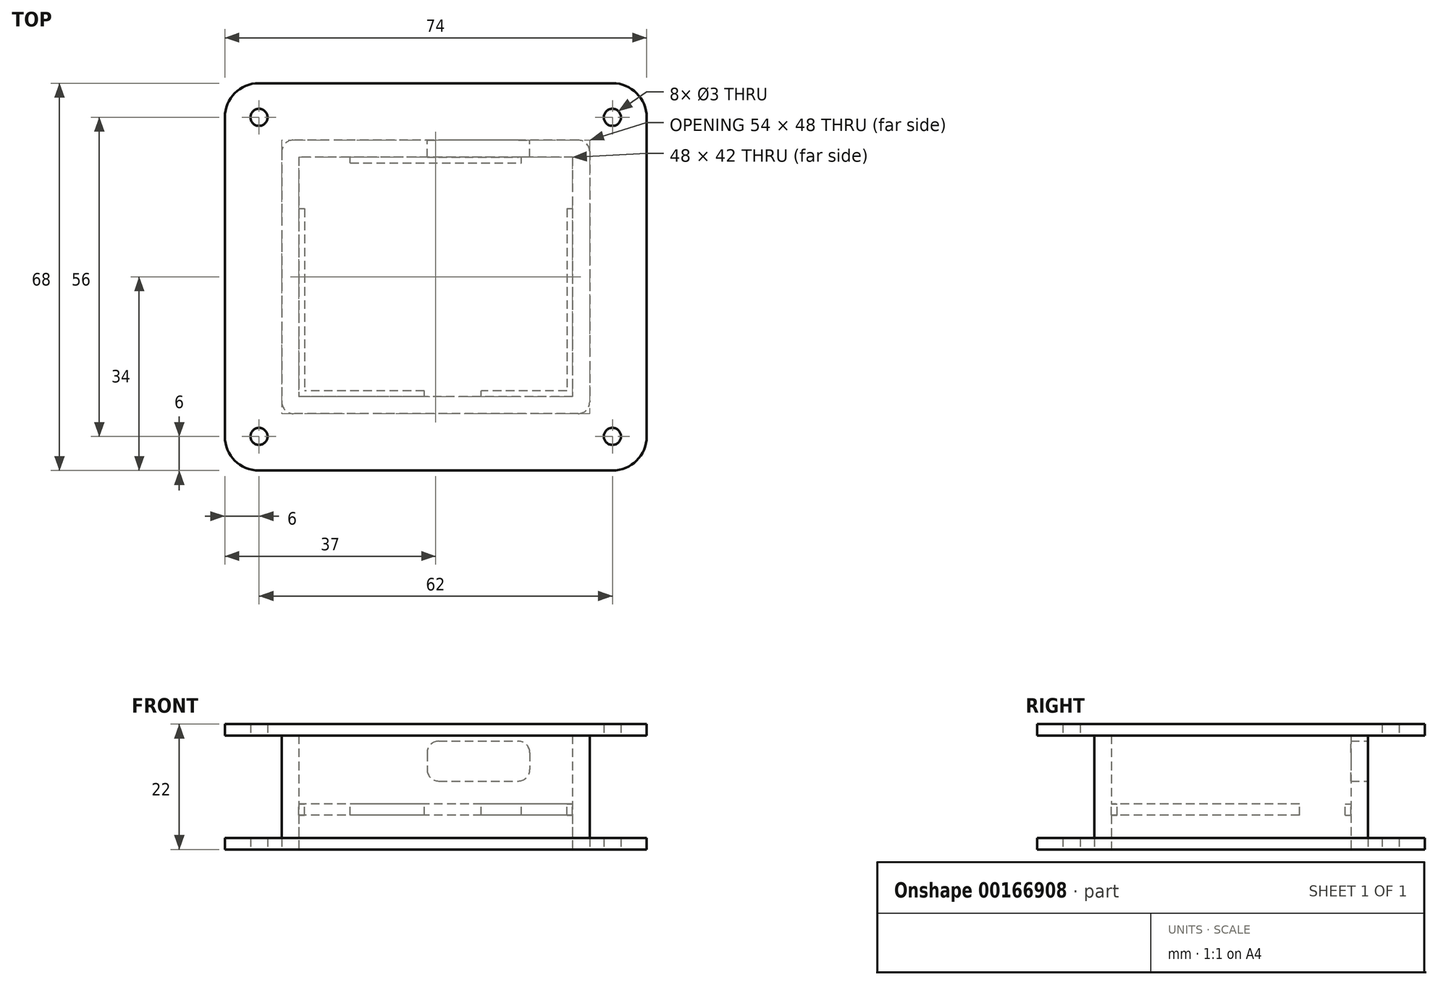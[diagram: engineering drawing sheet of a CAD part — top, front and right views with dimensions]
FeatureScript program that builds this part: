
annotation { "Feature Type Name" : "Feature", "Feature Type Description" : "" }
export const myFeature = defineFeature(function(context is Context, id is Id, definition is map)
    precondition{}
    {
        {
            var Q0;
            Q0=qCreatedBy(makeId("Top.planeOp"),FACE);
            var sketch = newSketch(context, id + "F0", { "sketchPlane" : qUnion([Q0])});
            skLineSegment(sketch, "E0.bottom", {"start": v(24, 21) * mm, "end": v(-24, 21) * mm});
            skLineSegment(sketch, "E0.top", {"start": v(24, -21) * mm, "end": v(-24, -21) * mm});
            skLineSegment(sketch, "E0.left", {"start": v(24, 21) * mm, "end": v(24, -21) * mm});
            skLineSegment(sketch, "E0.right", {"start": v(-24, 21) * mm, "end": v(-24, -21) * mm});
            skPoint(sketch, "E0.middle", {"position": v(0, 0) * mm});
            skLineSegment(sketch, "E1.0", {"start": v(-27, 22) * mm, "end": v(-27, -22) * mm});
            skLineSegment(sketch, "E1.1", {"start": v(25, 24) * mm, "end": v(-25, 24) * mm});
            skLineSegment(sketch, "E1.2", {"start": v(27, 22) * mm, "end": v(27, -22) * mm});
            skLineSegment(sketch, "E1.3", {"start": v(25, -24) * mm, "end": v(-25, -24) * mm});
            skPoint(sketch, "E2.visualSharp", {"position": v(-27, 24) * mm});
            skArc(sketch, "E2.filletArc", {"start": v(-25, 24) * mm, "mid": v(-26.41, 23.41) * mm, "end": v(-27, 22) * mm});
            skPoint(sketch, "E3.visualSharp", {"position": v(-27, -24) * mm});
            skArc(sketch, "E3.filletArc", {"start": v(-27, -22) * mm, "mid": v(-26.41, -23.41) * mm, "end": v(-25, -24) * mm});
            skPoint(sketch, "E4.visualSharp", {"position": v(27, -24) * mm});
            skArc(sketch, "E4.filletArc", {"start": v(25, -24) * mm, "mid": v(26.41, -23.41) * mm, "end": v(27, -22) * mm});
            skPoint(sketch, "E5.visualSharp", {"position": v(27, 24) * mm});
            skArc(sketch, "E5.filletArc", {"start": v(27, 22) * mm, "mid": v(26.41, 23.41) * mm, "end": v(25, 24) * mm});
            skSolve(sketch);
        }
        {
            var Q0;
            Q0 = qSketchRegion(id + "F0", true);
            extrude(context, id + "F1", {"entities" : qUnion([Q0]), "depth" : 20 * mm});
        }
        {
            var Q0;
            Q0=makeQuery(id+"F1.opExtrude","SWEPT_FACE",FACE,{"disambiguationData":[OSD([sQuery(id+"F0.wireOp",EDGE,"E1.1")])]});
            var sketch = newSketch(context, id + "F2", { "sketchPlane" : qUnion([Q0])});
            skLineSegment(sketch, "E6", {"start": v(-32.33, 8) * mm, "end": v(34.44, 8) * mm, "construction": true});
            skLineSegment(sketch, "E7", {"start": v(-32.34, 10) * mm, "end": v(33.7, 10) * mm, "construction": true});
            skLineSegment(sketch, "E8.bottom", {"start": v(-14.5, 12) * mm, "end": v(-0.5, 12) * mm});
            skLineSegment(sketch, "E8.top", {"start": v(-14.5, 19) * mm, "end": v(-0.5, 19) * mm});
            skLineSegment(sketch, "E8.left", {"start": v(-16.5, 14) * mm, "end": v(-16.5, 17) * mm});
            skLineSegment(sketch, "E8.right", {"start": v(1.5, 14) * mm, "end": v(1.5, 17) * mm});
            skLineSegment(sketch, "E9", {"start": v(-16.5, 19) * mm, "end": v(1.5, 12) * mm, "construction": true});
            skLineSegment(sketch, "E10", {"start": v(-16.5, 12) * mm, "end": v(1.5, 19) * mm, "construction": true});
            skPoint(sketch, "E11", {"position": v(-7.5, 15.5) * mm});
            skPoint(sketch, "E12.visualSharp", {"position": v(-16.5, 19) * mm});
            skArc(sketch, "E12.filletArc", {"start": v(-14.5, 19) * mm, "mid": v(-15.91, 18.41) * mm, "end": v(-16.5, 17) * mm});
            skPoint(sketch, "E13.visualSharp", {"position": v(-16.5, 12) * mm});
            skArc(sketch, "E13.filletArc", {"start": v(-16.5, 14) * mm, "mid": v(-15.91, 12.59) * mm, "end": v(-14.5, 12) * mm});
            skPoint(sketch, "E14.visualSharp", {"position": v(1.5, 12) * mm});
            skArc(sketch, "E14.filletArc", {"start": v(-0.5, 12) * mm, "mid": v(0.91, 12.59) * mm, "end": v(1.5, 14) * mm});
            skPoint(sketch, "E15.visualSharp", {"position": v(1.5, 19) * mm});
            skArc(sketch, "E15.filletArc", {"start": v(1.5, 17) * mm, "mid": v(0.91, 18.41) * mm, "end": v(-0.5, 19) * mm});
            skSolve(sketch);
        }
        {
            var Q0;
            Q0 = qSketchRegion(id + "F2", true);
            extrude(context, id + "F3", {"entities" : qUnion([Q0]), "operationType" : NewBodyOperationType.REMOVE, "oppositeDirection" : true, "depth" : 25 * mm});
        }
        {
            var Q0;
            Q0=makeQuery(id+"F1.opExtrude","CAP_FACE",FACE,{"disambiguationData":[OSD([sQuery(id+"F0.wireOp",EDGE,"E0.bottom"),sQuery(id+"F0.wireOp",EDGE,"E0.top"),sQuery(id+"F0.wireOp",EDGE,"E0.left"),sQuery(id+"F0.wireOp",EDGE,"E0.right"),sQuery(id+"F0.wireOp",EDGE,"E1.0"),sQuery(id+"F0.wireOp",EDGE,"E1.1"),sQuery(id+"F0.wireOp",EDGE,"E1.2"),sQuery(id+"F0.wireOp",EDGE,"E1.3"),sQuery(id+"F0.wireOp",EDGE,"E2.filletArc"),sQuery(id+"F0.wireOp",EDGE,"E3.filletArc"),sQuery(id+"F0.wireOp",EDGE,"E4.filletArc"),sQuery(id+"F0.wireOp",EDGE,"E5.filletArc")])],"isStart":false});
            cPlane(context, id + "F4", {"entities" : qUnion([Q0]), "cplaneType" : CPlaneType.OFFSET, "offset" : 12 * mm, "oppositeDirection" : true, "width" : 150 * mm, "height" : 150 * mm});
        }
        {
            var Q0;
            Q0=qCreatedBy(id+"F4.planeOp",FACE);
            var sketch = newSketch(context, id + "F5", { "sketchPlane" : qUnion([Q0])});
            skLineSegment(sketch, "E16.0", {"start": v(24, 12) * mm, "end": v(24, -21) * mm});
            skLineSegment(sketch, "E16.1", {"start": v(24, -21) * mm, "end": v(8, -21) * mm});
            skLineSegment(sketch, "E16.2", {"start": v(15, 21) * mm, "end": v(-15, 21) * mm});
            skLineSegment(sketch, "E16.3", {"start": v(-24, 12) * mm, "end": v(-24, -21) * mm});
            skLineSegment(sketch, "E17.0", {"start": v(23, -20) * mm, "end": v(8, -20) * mm});
            skLineSegment(sketch, "E17.1", {"start": v(23, 12) * mm, "end": v(23, -20) * mm});
            skLineSegment(sketch, "E17.3", {"start": v(-23, 12) * mm, "end": v(-23, -20) * mm});
            skLineSegment(sketch, "E18", {"start": v(-24, 12) * mm, "end": v(-23, 12) * mm});
            skLineSegment(sketch, "E19", {"start": v(23, 12) * mm, "end": v(24, 12) * mm});
            skLineSegment(sketch, "E20", {"start": v(-15, 20) * mm, "end": v(-15, 21) * mm});
            skLineSegment(sketch, "E21", {"start": v(15, 20) * mm, "end": v(15, 21) * mm});
            skPoint(sketch, "E22.orphan", {"position": v(-24, 21) * mm});
            skPoint(sketch, "E23.orphan", {"position": v(24, 21) * mm});
            skLineSegment(sketch, "E24", {"start": v(-15, 20) * mm, "end": v(15, 20) * mm});
            skLineSegment(sketch, "E25.left", {"start": v(8, -21) * mm, "end": v(8, -20) * mm});
            skLineSegment(sketch, "E25.right", {"start": v(-2, -21) * mm, "end": v(-2, -20) * mm});
            skPoint(sketch, "E25.middle", {"position": v(3, -14.9) * mm});
            skLineSegment(sketch, "E26.trimOffspring", {"start": v(-2, -20) * mm, "end": v(-23, -20) * mm});
            skLineSegment(sketch, "E27.trimOffspring", {"start": v(-2, -21) * mm, "end": v(-24, -21) * mm});
            skPoint(sketch, "E25.top.end.orphan", {"position": v(-2, -8.05) * mm});
            skPoint(sketch, "E28.orphan", {"position": v(8, -8.05) * mm});
            skPoint(sketch, "E29.orphan", {"position": v(-2, -21.76) * mm});
            skPoint(sketch, "E30.orphan", {"position": v(8, -21.76) * mm});
            skSolve(sketch);
        }
        {
            var Q0;
            Q0 = qSketchRegion(id + "F5", true);
            extrude(context, id + "F6", {"entities" : qUnion([Q0]), "operationType" : NewBodyOperationType.ADD, "oppositeDirection" : true, "depth" : 2 * mm});
        }
        {
            var Q0;
            Q0=makeQuery(id+"F1.opExtrude","CAP_FACE",FACE,{"disambiguationData":[OSD([sQuery(id+"F0.wireOp",EDGE,"E0.bottom"),sQuery(id+"F0.wireOp",EDGE,"E0.top"),sQuery(id+"F0.wireOp",EDGE,"E0.left"),sQuery(id+"F0.wireOp",EDGE,"E0.right"),sQuery(id+"F0.wireOp",EDGE,"E1.0"),sQuery(id+"F0.wireOp",EDGE,"E1.1"),sQuery(id+"F0.wireOp",EDGE,"E1.2"),sQuery(id+"F0.wireOp",EDGE,"E1.3"),sQuery(id+"F0.wireOp",EDGE,"E2.filletArc"),sQuery(id+"F0.wireOp",EDGE,"E3.filletArc"),sQuery(id+"F0.wireOp",EDGE,"E4.filletArc"),sQuery(id+"F0.wireOp",EDGE,"E5.filletArc")])],"isStart":false});
            var sketch = newSketch(context, id + "F7", { "sketchPlane" : qUnion([Q0])});
            skLineSegment(sketch, "E31.bottom", {"start": v(31, 34) * mm, "end": v(-31, 34) * mm});
            skLineSegment(sketch, "E31.top", {"start": v(31, -34) * mm, "end": v(-31, -34) * mm});
            skLineSegment(sketch, "E31.left", {"start": v(37, 28) * mm, "end": v(37, -28) * mm});
            skLineSegment(sketch, "E31.right", {"start": v(-37, 28) * mm, "end": v(-37, -28) * mm});
            skPoint(sketch, "E31.middle", {"position": v(0, 0) * mm});
            skPoint(sketch, "E32.visualSharp", {"position": v(-37, 34) * mm});
            skArc(sketch, "E32.filletArc", {"start": v(-31, 34) * mm, "mid": v(-35.24, 32.24) * mm, "end": v(-37, 28) * mm});
            skPoint(sketch, "E33.visualSharp", {"position": v(-37, -34) * mm});
            skArc(sketch, "E33.filletArc", {"start": v(-37, -28) * mm, "mid": v(-35.24, -32.24) * mm, "end": v(-31, -34) * mm});
            skPoint(sketch, "E34.visualSharp", {"position": v(37, -34) * mm});
            skArc(sketch, "E34.filletArc", {"start": v(31, -34) * mm, "mid": v(35.24, -32.24) * mm, "end": v(37, -28) * mm});
            skPoint(sketch, "E35.visualSharp", {"position": v(37, 34) * mm});
            skArc(sketch, "E35.filletArc", {"start": v(37, 28) * mm, "mid": v(35.24, 32.24) * mm, "end": v(31, 34) * mm});
            skCircle(sketch, "E36", {"center": v(-31, 28) * mm, "radius": 1.5 * mm});
            skCircle(sketch, "E37", {"center": v(31, 28) * mm, "radius": 1.5 * mm});
            skCircle(sketch, "E38", {"center": v(31, -28) * mm, "radius": 1.5 * mm});
            skCircle(sketch, "E39", {"center": v(-31, -28) * mm, "radius": 1.5 * mm});
            skSolve(sketch);
        }
        {
            var Q0;
            Q0 = qSketchRegion(id + "F7", true);
            extrude(context, id + "F8", {"entities" : qUnion([Q0]), "depth" : 2 * mm});
        }
        {
            var Q0;
            Q0=makeQuery(id+"F1.opExtrude","CAP_FACE",FACE,{"disambiguationData":[OSD([sQuery(id+"F0.wireOp",EDGE,"E0.bottom"),sQuery(id+"F0.wireOp",EDGE,"E0.top"),sQuery(id+"F0.wireOp",EDGE,"E0.left"),sQuery(id+"F0.wireOp",EDGE,"E0.right"),sQuery(id+"F0.wireOp",EDGE,"E1.0"),sQuery(id+"F0.wireOp",EDGE,"E1.1"),sQuery(id+"F0.wireOp",EDGE,"E1.2"),sQuery(id+"F0.wireOp",EDGE,"E1.3"),sQuery(id+"F0.wireOp",EDGE,"E2.filletArc"),sQuery(id+"F0.wireOp",EDGE,"E3.filletArc"),sQuery(id+"F0.wireOp",EDGE,"E4.filletArc"),sQuery(id+"F0.wireOp",EDGE,"E5.filletArc")])],"isStart":true});
            var sketch = newSketch(context, id + "F9", { "sketchPlane" : qUnion([Q0])});
            skLineSegment(sketch, "E40.0", {"start": v(27, -22) * mm, "end": v(27, 22) * mm});
            skArc(sketch, "E40.1", {"start": v(27, -22) * mm, "mid": v(26.41, -23.41) * mm, "end": v(25, -24) * mm});
            skLineSegment(sketch, "E40.2", {"start": v(25, -24) * mm, "end": v(-25, -24) * mm});
            skArc(sketch, "E40.3", {"start": v(-25, -24) * mm, "mid": v(-26.41, -23.41) * mm, "end": v(-27, -22) * mm});
            skLineSegment(sketch, "E40.4", {"start": v(-27, -22) * mm, "end": v(-27, 22) * mm});
            skArc(sketch, "E40.5", {"start": v(-27, 22) * mm, "mid": v(-26.41, 23.41) * mm, "end": v(-25, 24) * mm});
            skLineSegment(sketch, "E40.6", {"start": v(25, 24) * mm, "end": v(-25, 24) * mm});
            skArc(sketch, "E40.7", {"start": v(25, 24) * mm, "mid": v(26.41, 23.41) * mm, "end": v(27, 22) * mm});
            skArc(sketch, "E41.0.0", {"start": v(31, -34) * mm, "mid": v(35.24, -32.24) * mm, "end": v(37, -28) * mm});
            skLineSegment(sketch, "E41.0.1", {"start": v(37, -28) * mm, "end": v(37, 28) * mm});
            skArc(sketch, "E41.0.2", {"start": v(37, 28) * mm, "mid": v(35.24, 32.24) * mm, "end": v(31, 34) * mm});
            skLineSegment(sketch, "E41.0.3", {"start": v(31, 34) * mm, "end": v(-31, 34) * mm});
            skArc(sketch, "E41.0.4", {"start": v(-31, 34) * mm, "mid": v(-35.24, 32.24) * mm, "end": v(-37, 28) * mm});
            skLineSegment(sketch, "E41.0.5", {"start": v(-37, 28) * mm, "end": v(-37, -28) * mm});
            skArc(sketch, "E41.0.6", {"start": v(-37, -28) * mm, "mid": v(-35.24, -32.24) * mm, "end": v(-31, -34) * mm});
            skLineSegment(sketch, "E41.0.7", {"start": v(-31, -34) * mm, "end": v(31, -34) * mm});
            skCircle(sketch, "E42", {"center": v(-31, 28) * mm, "radius": 1.5 * mm});
            skLineSegment(sketch, "E43", {"start": v(0, 0) * mm, "end": v(0, 6.93) * mm, "construction": true});
            skLineSegment(sketch, "E44", {"start": v(0, 0) * mm, "end": v(-6.6, 0) * mm, "construction": true});
            skCircle(sketch, "E45.MirrorC", {"center": v(31, 28) * mm, "radius": 1.5 * mm});
            skCircle(sketch, "E46.MirrorC", {"center": v(-31, -28) * mm, "radius": 1.5 * mm});
            skCircle(sketch, "E47.MirrorC", {"center": v(31, -28) * mm, "radius": 1.5 * mm});
            skSolve(sketch);
        }
        {
            var Q0;
            Q0 = qSketchRegion(id + "F9", true);
            extrude(context, id + "F10", {"entities" : qUnion([Q0]), "oppositeDirection" : true, "depth" : 2 * mm});
        }
    });
